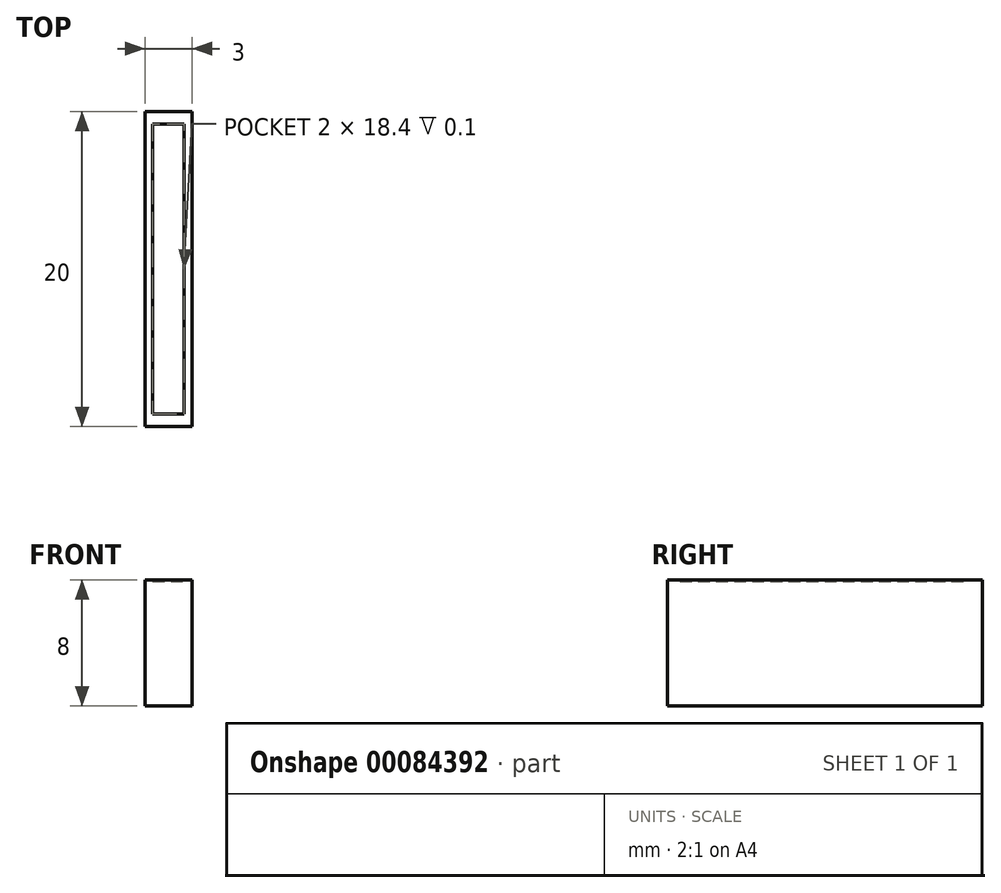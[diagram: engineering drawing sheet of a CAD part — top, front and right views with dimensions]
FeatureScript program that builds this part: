
annotation { "Feature Type Name" : "Feature", "Feature Type Description" : "" }
export const myFeature = defineFeature(function(context is Context, id is Id, definition is map)
    precondition{}
    {
        {
            var Q0;
            Q0=qCreatedBy(makeId("Top.planeOp"),FACE);
            var sketch = newSketch(context, id + "F0", { "sketchPlane" : qUnion([Q0])});
            skLineSegment(sketch, "E0.bottom", {"start": v(-53.44, 15.74) * mm, "end": v(-50.44, 15.74) * mm});
            skLineSegment(sketch, "E0.top", {"start": v(-53.44, -4.26) * mm, "end": v(-50.44, -4.26) * mm});
            skLineSegment(sketch, "E0.left", {"start": v(-53.44, 15.74) * mm, "end": v(-53.44, -4.26) * mm});
            skLineSegment(sketch, "E0.right", {"start": v(-50.44, 15.74) * mm, "end": v(-50.44, -4.26) * mm});
            skLineSegment(sketch, "E1", {"start": v(-50.94, -4.26) * mm, "end": v(-50.94, 15.74) * mm});
            skLineSegment(sketch, "E2", {"start": v(-52.94, -4.26) * mm, "end": v(-52.94, 15.74) * mm});
            skLineSegment(sketch, "E3", {"start": v(-52.94, -3.46) * mm, "end": v(-50.94, -3.46) * mm});
            skLineSegment(sketch, "E4", {"start": v(-52.94, -1.86) * mm, "end": v(-50.94, -1.86) * mm});
            skLineSegment(sketch, "E5", {"start": v(-52.94, -1.06) * mm, "end": v(-50.94, -1.06) * mm});
            skLineSegment(sketch, "E6", {"start": v(-52.94, 0.54) * mm, "end": v(-50.94, 0.54) * mm});
            skLineSegment(sketch, "E7", {"start": v(-52.94, 1.34) * mm, "end": v(-50.94, 1.34) * mm});
            skLineSegment(sketch, "E8", {"start": v(-52.94, 2.94) * mm, "end": v(-50.94, 2.94) * mm});
            skLineSegment(sketch, "E9", {"start": v(-52.94, 3.74) * mm, "end": v(-50.94, 3.74) * mm});
            skLineSegment(sketch, "E10", {"start": v(-52.94, 5.34) * mm, "end": v(-50.94, 5.34) * mm});
            skLineSegment(sketch, "E11", {"start": v(-52.94, 6.14) * mm, "end": v(-50.94, 6.14) * mm});
            skLineSegment(sketch, "E12", {"start": v(-52.94, 7.74) * mm, "end": v(-50.94, 7.74) * mm});
            skLineSegment(sketch, "E13", {"start": v(-52.94, 8.54) * mm, "end": v(-50.94, 8.54) * mm});
            skLineSegment(sketch, "E14", {"start": v(-52.94, 10.14) * mm, "end": v(-50.94, 10.14) * mm});
            skLineSegment(sketch, "E15", {"start": v(-52.94, 10.94) * mm, "end": v(-50.94, 10.94) * mm});
            skLineSegment(sketch, "E16", {"start": v(-52.94, 12.54) * mm, "end": v(-50.94, 12.54) * mm});
            skLineSegment(sketch, "E17", {"start": v(-52.94, 13.34) * mm, "end": v(-50.94, 13.34) * mm});
            skLineSegment(sketch, "E18", {"start": v(-52.94, 14.94) * mm, "end": v(-50.94, 14.94) * mm});
            skLineSegment(sketch, "E19", {"start": v(-52.94, 15.74) * mm, "end": v(-50.94, 15.74) * mm});
            skLineSegment(sketch, "E20", {"start": v(-52.94, -3.06) * mm, "end": v(-50.94, -3.06) * mm});
            skLineSegment(sketch, "E21", {"start": v(-52.94, -2.26) * mm, "end": v(-50.94, -2.26) * mm});
            skLineSegment(sketch, "E22", {"start": v(-52.54, -4.26) * mm, "end": v(-52.54, 15.74) * mm});
            skLineSegment(sketch, "E23", {"start": v(-51.34, -4.26) * mm, "end": v(-51.34, 15.74) * mm});
            skLineSegment(sketch, "E24", {"start": v(-51.34, 15.74) * mm, "end": v(-51.55, 15.82) * mm});
            skLineSegment(sketch, "E25", {"start": v(-52.94, -0.66) * mm, "end": v(-50.94, -0.66) * mm});
            skLineSegment(sketch, "E26", {"start": v(-52.94, 0.14) * mm, "end": v(-50.94, 0.14) * mm});
            skLineSegment(sketch, "E27", {"start": v(-52.94, 1.74) * mm, "end": v(-50.94, 1.74) * mm});
            skLineSegment(sketch, "E28", {"start": v(-52.94, 2.54) * mm, "end": v(-50.94, 2.54) * mm});
            skLineSegment(sketch, "E29", {"start": v(-52.94, 4.14) * mm, "end": v(-50.94, 4.14) * mm});
            skLineSegment(sketch, "E30", {"start": v(-52.94, 4.94) * mm, "end": v(-50.94, 4.94) * mm});
            skLineSegment(sketch, "E31", {"start": v(-52.94, 6.54) * mm, "end": v(-50.94, 6.54) * mm});
            skLineSegment(sketch, "E32", {"start": v(-52.94, 8.94) * mm, "end": v(-50.94, 8.94) * mm});
            skLineSegment(sketch, "E33", {"start": v(-52.94, 9.74) * mm, "end": v(-50.94, 9.74) * mm});
            skLineSegment(sketch, "E34", {"start": v(-52.94, 11.34) * mm, "end": v(-50.94, 11.34) * mm});
            skLineSegment(sketch, "E35", {"start": v(-50.94, 11.34) * mm, "end": v(-50.9, 11.2) * mm});
            skLineSegment(sketch, "E36", {"start": v(-52.94, 12.14) * mm, "end": v(-50.94, 12.14) * mm});
            skLineSegment(sketch, "E37", {"start": v(-52.94, 13.74) * mm, "end": v(-50.94, 13.74) * mm});
            skLineSegment(sketch, "E38", {"start": v(-52.94, 14.54) * mm, "end": v(-50.94, 14.54) * mm});
            skLineSegment(sketch, "E39", {"start": v(-52.94, 7.34) * mm, "end": v(-50.94, 7.34) * mm});
            skSolve(sketch);
        }
        {
            var Q0;
            Q0 = qSketchRegion(id + "F0", true);
            extrude(context, id + "F1", {"entities" : qUnion([Q0]), "depth" : 8 * mm});
        }
        {
            var Q0;
            {var subQ0=sQuery(id+"F0.wireOp",EDGE,"E18");var subQ1=sQuery(id+"F0.wireOp",EDGE,"E2");var subQ2=makeQuery(id+"F0.imprint","INTERSECT",VERTEX,{"derivedFrom":[subQ1,subQ0]});Q0=makeQuery(id+"F0.imprint","IMPRINT",FACE,{"disambiguationData":[TD([[makeQuery(id+"F0.imprint","IMPRINT",EDGE,{"disambiguationData":[TD([[subQ2,1.0]])],"derivedFrom":subQ1}),-1.0]])]});}
            var Q1;
            {var subQ0=sQuery(id+"F0.wireOp",EDGE,"E37");var subQ1=sQuery(id+"F0.wireOp",EDGE,"E2");var subQ2=makeQuery(id+"F0.imprint","INTERSECT",VERTEX,{"derivedFrom":[subQ1,subQ0]});Q1=makeQuery(id+"F0.imprint","IMPRINT",FACE,{"disambiguationData":[TD([[makeQuery(id+"F0.imprint","IMPRINT",EDGE,{"disambiguationData":[TD([[subQ2,-1.0]])],"derivedFrom":subQ1}),-1.0]])]});}
            var Q2;
            {var subQ0=sQuery(id+"F0.wireOp",EDGE,"E17");var subQ1=sQuery(id+"F0.wireOp",EDGE,"E2");var subQ2=makeQuery(id+"F0.imprint","INTERSECT",VERTEX,{"derivedFrom":[subQ1,subQ0]});Q2=makeQuery(id+"F0.imprint","IMPRINT",FACE,{"disambiguationData":[TD([[makeQuery(id+"F0.imprint","IMPRINT",EDGE,{"disambiguationData":[TD([[subQ2,-1.0]])],"derivedFrom":subQ1}),-1.0]])]});}
            var Q3;
            {var subQ0=sQuery(id+"F0.wireOp",EDGE,"E16");var subQ1=sQuery(id+"F0.wireOp",EDGE,"E2");var subQ2=makeQuery(id+"F0.imprint","INTERSECT",VERTEX,{"derivedFrom":[subQ1,subQ0]});Q3=makeQuery(id+"F0.imprint","IMPRINT",FACE,{"disambiguationData":[TD([[makeQuery(id+"F0.imprint","IMPRINT",EDGE,{"disambiguationData":[TD([[subQ2,-1.0]])],"derivedFrom":subQ1}),-1.0]])]});}
            var Q4;
            {var subQ0=sQuery(id+"F0.wireOp",EDGE,"E16");var subQ1=sQuery(id+"F0.wireOp",EDGE,"E2");var subQ2=makeQuery(id+"F0.imprint","INTERSECT",VERTEX,{"derivedFrom":[subQ1,subQ0]});Q4=makeQuery(id+"F0.imprint","IMPRINT",FACE,{"disambiguationData":[TD([[makeQuery(id+"F0.imprint","IMPRINT",EDGE,{"disambiguationData":[TD([[subQ2,1.0]])],"derivedFrom":subQ1}),-1.0]])]});}
            var Q5;
            {var subQ0=sQuery(id+"F0.wireOp",EDGE,"E34");var subQ1=sQuery(id+"F0.wireOp",EDGE,"E2");var subQ2=makeQuery(id+"F0.imprint","INTERSECT",VERTEX,{"derivedFrom":[subQ1,subQ0]});Q5=makeQuery(id+"F0.imprint","IMPRINT",FACE,{"disambiguationData":[TD([[makeQuery(id+"F0.imprint","IMPRINT",EDGE,{"disambiguationData":[TD([[subQ2,-1.0]])],"derivedFrom":subQ1}),-1.0]])]});}
            var Q6;
            {var subQ0=sQuery(id+"F0.wireOp",EDGE,"E15");var subQ1=sQuery(id+"F0.wireOp",EDGE,"E2");var subQ2=makeQuery(id+"F0.imprint","INTERSECT",VERTEX,{"derivedFrom":[subQ1,subQ0]});Q6=makeQuery(id+"F0.imprint","IMPRINT",FACE,{"disambiguationData":[TD([[makeQuery(id+"F0.imprint","IMPRINT",EDGE,{"disambiguationData":[TD([[subQ2,-1.0]])],"derivedFrom":subQ1}),-1.0]])]});}
            var Q7;
            {var subQ0=sQuery(id+"F0.wireOp",EDGE,"E14");var subQ1=sQuery(id+"F0.wireOp",EDGE,"E2");var subQ2=makeQuery(id+"F0.imprint","INTERSECT",VERTEX,{"derivedFrom":[subQ1,subQ0]});Q7=makeQuery(id+"F0.imprint","IMPRINT",FACE,{"disambiguationData":[TD([[makeQuery(id+"F0.imprint","IMPRINT",EDGE,{"disambiguationData":[TD([[subQ2,-1.0]])],"derivedFrom":subQ1}),-1.0]])]});}
            var Q8;
            {var subQ0=sQuery(id+"F0.wireOp",EDGE,"E14");var subQ1=sQuery(id+"F0.wireOp",EDGE,"E2");var subQ2=makeQuery(id+"F0.imprint","INTERSECT",VERTEX,{"derivedFrom":[subQ1,subQ0]});Q8=makeQuery(id+"F0.imprint","IMPRINT",FACE,{"disambiguationData":[TD([[makeQuery(id+"F0.imprint","IMPRINT",EDGE,{"disambiguationData":[TD([[subQ2,1.0]])],"derivedFrom":subQ1}),-1.0]])]});}
            var Q9;
            {var subQ0=sQuery(id+"F0.wireOp",EDGE,"E22");var subQ1=sQuery(id+"F0.wireOp",EDGE,"E14");var subQ2=makeQuery(id+"F0.imprint","INTERSECT",VERTEX,{"derivedFrom":[subQ1,subQ0]});Q9=makeQuery(id+"F0.imprint","IMPRINT",FACE,{"disambiguationData":[TD([[makeQuery(id+"F0.imprint","IMPRINT",EDGE,{"disambiguationData":[TD([[subQ2,-1.0]])],"derivedFrom":subQ1}),-1.0]])]});}
            var Q10;
            {var subQ0=sQuery(id+"F0.wireOp",EDGE,"E22");var subQ1=sQuery(id+"F0.wireOp",EDGE,"E15");var subQ2=makeQuery(id+"F0.imprint","INTERSECT",VERTEX,{"derivedFrom":[subQ1,subQ0]});Q10=makeQuery(id+"F0.imprint","IMPRINT",FACE,{"disambiguationData":[TD([[makeQuery(id+"F0.imprint","IMPRINT",EDGE,{"disambiguationData":[TD([[subQ2,-1.0]])],"derivedFrom":subQ1}),1.0]])]});}
            var Q11;
            {var subQ0=sQuery(id+"F0.wireOp",EDGE,"E22");var subQ1=sQuery(id+"F0.wireOp",EDGE,"E16");var subQ2=makeQuery(id+"F0.imprint","INTERSECT",VERTEX,{"derivedFrom":[subQ1,subQ0]});Q11=makeQuery(id+"F0.imprint","IMPRINT",FACE,{"disambiguationData":[TD([[makeQuery(id+"F0.imprint","IMPRINT",EDGE,{"disambiguationData":[TD([[subQ2,-1.0]])],"derivedFrom":subQ1}),-1.0]])]});}
            var Q12;
            {var subQ0=sQuery(id+"F0.wireOp",EDGE,"E22");var subQ1=sQuery(id+"F0.wireOp",EDGE,"E17");var subQ2=makeQuery(id+"F0.imprint","INTERSECT",VERTEX,{"derivedFrom":[subQ1,subQ0]});Q12=makeQuery(id+"F0.imprint","IMPRINT",FACE,{"disambiguationData":[TD([[makeQuery(id+"F0.imprint","IMPRINT",EDGE,{"disambiguationData":[TD([[subQ2,-1.0]])],"derivedFrom":subQ1}),1.0]])]});}
            var Q13;
            {var subQ0=sQuery(id+"F0.wireOp",EDGE,"E22");var subQ1=sQuery(id+"F0.wireOp",EDGE,"E18");var subQ2=makeQuery(id+"F0.imprint","INTERSECT",VERTEX,{"derivedFrom":[subQ1,subQ0]});Q13=makeQuery(id+"F0.imprint","IMPRINT",FACE,{"disambiguationData":[TD([[makeQuery(id+"F0.imprint","IMPRINT",EDGE,{"disambiguationData":[TD([[subQ2,-1.0]])],"derivedFrom":subQ1}),-1.0]])]});}
            var Q14;
            {var subQ0=sQuery(id+"F0.wireOp",EDGE,"E22");var subQ1=sQuery(id+"F0.wireOp",EDGE,"E3");var subQ2=makeQuery(id+"F0.imprint","INTERSECT",VERTEX,{"derivedFrom":[subQ1,subQ0]});Q14=makeQuery(id+"F0.imprint","IMPRINT",FACE,{"disambiguationData":[TD([[makeQuery(id+"F0.imprint","IMPRINT",EDGE,{"disambiguationData":[TD([[subQ2,-1.0]])],"derivedFrom":subQ1}),1.0]])]});}
            var Q15;
            {var subQ0=sQuery(id+"F0.wireOp",EDGE,"E22");var subQ1=sQuery(id+"F0.wireOp",EDGE,"E4");var subQ2=makeQuery(id+"F0.imprint","INTERSECT",VERTEX,{"derivedFrom":[subQ1,subQ0]});Q15=makeQuery(id+"F0.imprint","IMPRINT",FACE,{"disambiguationData":[TD([[makeQuery(id+"F0.imprint","IMPRINT",EDGE,{"disambiguationData":[TD([[subQ2,-1.0]])],"derivedFrom":subQ1}),-1.0]])]});}
            var Q16;
            {var subQ0=sQuery(id+"F0.wireOp",EDGE,"E22");var subQ1=sQuery(id+"F0.wireOp",EDGE,"E5");var subQ2=makeQuery(id+"F0.imprint","INTERSECT",VERTEX,{"derivedFrom":[subQ1,subQ0]});Q16=makeQuery(id+"F0.imprint","IMPRINT",FACE,{"disambiguationData":[TD([[makeQuery(id+"F0.imprint","IMPRINT",EDGE,{"disambiguationData":[TD([[subQ2,-1.0]])],"derivedFrom":subQ1}),1.0]])]});}
            var Q17;
            {var subQ0=sQuery(id+"F0.wireOp",EDGE,"E22");var subQ1=sQuery(id+"F0.wireOp",EDGE,"E6");var subQ2=makeQuery(id+"F0.imprint","INTERSECT",VERTEX,{"derivedFrom":[subQ1,subQ0]});Q17=makeQuery(id+"F0.imprint","IMPRINT",FACE,{"disambiguationData":[TD([[makeQuery(id+"F0.imprint","IMPRINT",EDGE,{"disambiguationData":[TD([[subQ2,-1.0]])],"derivedFrom":subQ1}),-1.0]])]});}
            var Q18;
            {var subQ0=sQuery(id+"F0.wireOp",EDGE,"E22");var subQ1=sQuery(id+"F0.wireOp",EDGE,"E7");var subQ2=makeQuery(id+"F0.imprint","INTERSECT",VERTEX,{"derivedFrom":[subQ1,subQ0]});Q18=makeQuery(id+"F0.imprint","IMPRINT",FACE,{"disambiguationData":[TD([[makeQuery(id+"F0.imprint","IMPRINT",EDGE,{"disambiguationData":[TD([[subQ2,-1.0]])],"derivedFrom":subQ1}),1.0]])]});}
            var Q19;
            {var subQ0=sQuery(id+"F0.wireOp",EDGE,"E22");var subQ1=sQuery(id+"F0.wireOp",EDGE,"E8");var subQ2=makeQuery(id+"F0.imprint","INTERSECT",VERTEX,{"derivedFrom":[subQ1,subQ0]});Q19=makeQuery(id+"F0.imprint","IMPRINT",FACE,{"disambiguationData":[TD([[makeQuery(id+"F0.imprint","IMPRINT",EDGE,{"disambiguationData":[TD([[subQ2,-1.0]])],"derivedFrom":subQ1}),-1.0]])]});}
            var Q20;
            {var subQ0=sQuery(id+"F0.wireOp",EDGE,"E9");var subQ1=sQuery(id+"F0.wireOp",EDGE,"E22");var subQ2=makeQuery(id+"F0.imprint","INTERSECT",VERTEX,{"derivedFrom":[subQ1,subQ0]});Q20=makeQuery(id+"F0.imprint","IMPRINT",FACE,{"disambiguationData":[TD([[makeQuery(id+"F0.imprint","IMPRINT",EDGE,{"disambiguationData":[TD([[subQ2,-1.0]])],"derivedFrom":subQ1}),-1.0]])]});}
            var Q21;
            {var subQ0=sQuery(id+"F0.wireOp",EDGE,"E22");var subQ1=sQuery(id+"F0.wireOp",EDGE,"E10");var subQ2=makeQuery(id+"F0.imprint","INTERSECT",VERTEX,{"derivedFrom":[subQ1,subQ0]});Q21=makeQuery(id+"F0.imprint","IMPRINT",FACE,{"disambiguationData":[TD([[makeQuery(id+"F0.imprint","IMPRINT",EDGE,{"disambiguationData":[TD([[subQ2,-1.0]])],"derivedFrom":subQ1}),-1.0]])]});}
            var Q22;
            {var subQ0=sQuery(id+"F0.wireOp",EDGE,"E22");var subQ1=sQuery(id+"F0.wireOp",EDGE,"E11");var subQ2=makeQuery(id+"F0.imprint","INTERSECT",VERTEX,{"derivedFrom":[subQ1,subQ0]});Q22=makeQuery(id+"F0.imprint","IMPRINT",FACE,{"disambiguationData":[TD([[makeQuery(id+"F0.imprint","IMPRINT",EDGE,{"disambiguationData":[TD([[subQ2,-1.0]])],"derivedFrom":subQ1}),1.0]])]});}
            var Q23;
            {var subQ0=sQuery(id+"F0.wireOp",EDGE,"E22");var subQ1=sQuery(id+"F0.wireOp",EDGE,"E12");var subQ2=makeQuery(id+"F0.imprint","INTERSECT",VERTEX,{"derivedFrom":[subQ1,subQ0]});Q23=makeQuery(id+"F0.imprint","IMPRINT",FACE,{"disambiguationData":[TD([[makeQuery(id+"F0.imprint","IMPRINT",EDGE,{"disambiguationData":[TD([[subQ2,-1.0]])],"derivedFrom":subQ1}),-1.0]])]});}
            var Q24;
            {var subQ0=sQuery(id+"F0.wireOp",EDGE,"E22");var subQ1=sQuery(id+"F0.wireOp",EDGE,"E13");var subQ2=makeQuery(id+"F0.imprint","INTERSECT",VERTEX,{"derivedFrom":[subQ1,subQ0]});Q24=makeQuery(id+"F0.imprint","IMPRINT",FACE,{"disambiguationData":[TD([[makeQuery(id+"F0.imprint","IMPRINT",EDGE,{"disambiguationData":[TD([[subQ2,-1.0]])],"derivedFrom":subQ1}),1.0]])]});}
            var Q25;
            {var subQ0=sQuery(id+"F0.wireOp",EDGE,"E18");var subQ1=sQuery(id+"F0.wireOp",EDGE,"E1");var subQ2=makeQuery(id+"F0.imprint","INTERSECT",VERTEX,{"derivedFrom":[subQ1,subQ0]});Q25=makeQuery(id+"F0.imprint","IMPRINT",FACE,{"disambiguationData":[TD([[makeQuery(id+"F0.imprint","IMPRINT",EDGE,{"disambiguationData":[TD([[subQ2,1.0]])],"derivedFrom":subQ1}),1.0]])]});}
            var Q26;
            {var subQ0=sQuery(id+"F0.wireOp",EDGE,"E17");var subQ1=sQuery(id+"F0.wireOp",EDGE,"E1");var subQ2=makeQuery(id+"F0.imprint","INTERSECT",VERTEX,{"derivedFrom":[subQ1,subQ0]});Q26=makeQuery(id+"F0.imprint","IMPRINT",FACE,{"disambiguationData":[TD([[makeQuery(id+"F0.imprint","IMPRINT",EDGE,{"disambiguationData":[TD([[subQ2,-1.0]])],"derivedFrom":subQ1}),1.0]])]});}
            var Q27;
            {var subQ0=sQuery(id+"F0.wireOp",EDGE,"E16");var subQ1=sQuery(id+"F0.wireOp",EDGE,"E1");var subQ2=makeQuery(id+"F0.imprint","INTERSECT",VERTEX,{"derivedFrom":[subQ1,subQ0]});Q27=makeQuery(id+"F0.imprint","IMPRINT",FACE,{"disambiguationData":[TD([[makeQuery(id+"F0.imprint","IMPRINT",EDGE,{"disambiguationData":[TD([[subQ2,1.0]])],"derivedFrom":subQ1}),1.0]])]});}
            var Q28;
            {var subQ0=sQuery(id+"F0.wireOp",EDGE,"E15");var subQ1=sQuery(id+"F0.wireOp",EDGE,"E1");var subQ2=makeQuery(id+"F0.imprint","INTERSECT",VERTEX,{"derivedFrom":[subQ1,subQ0]});Q28=makeQuery(id+"F0.imprint","IMPRINT",FACE,{"disambiguationData":[TD([[makeQuery(id+"F0.imprint","IMPRINT",EDGE,{"disambiguationData":[TD([[subQ2,-1.0]])],"derivedFrom":subQ1}),1.0]])]});}
            var Q29;
            {var subQ0=sQuery(id+"F0.wireOp",EDGE,"E14");var subQ1=sQuery(id+"F0.wireOp",EDGE,"E1");var subQ2=makeQuery(id+"F0.imprint","INTERSECT",VERTEX,{"derivedFrom":[subQ1,subQ0]});Q29=makeQuery(id+"F0.imprint","IMPRINT",FACE,{"disambiguationData":[TD([[makeQuery(id+"F0.imprint","IMPRINT",EDGE,{"disambiguationData":[TD([[subQ2,1.0]])],"derivedFrom":subQ1}),1.0]])]});}
            var Q30;
            {var subQ0=sQuery(id+"F0.wireOp",EDGE,"E13");var subQ1=sQuery(id+"F0.wireOp",EDGE,"E1");var subQ2=makeQuery(id+"F0.imprint","INTERSECT",VERTEX,{"derivedFrom":[subQ1,subQ0]});Q30=makeQuery(id+"F0.imprint","IMPRINT",FACE,{"disambiguationData":[TD([[makeQuery(id+"F0.imprint","IMPRINT",EDGE,{"disambiguationData":[TD([[subQ2,-1.0]])],"derivedFrom":subQ1}),1.0]])]});}
            var Q31;
            {var subQ0=sQuery(id+"F0.wireOp",EDGE,"E12");var subQ1=sQuery(id+"F0.wireOp",EDGE,"E1");var subQ2=makeQuery(id+"F0.imprint","INTERSECT",VERTEX,{"derivedFrom":[subQ1,subQ0]});Q31=makeQuery(id+"F0.imprint","IMPRINT",FACE,{"disambiguationData":[TD([[makeQuery(id+"F0.imprint","IMPRINT",EDGE,{"disambiguationData":[TD([[subQ2,1.0]])],"derivedFrom":subQ1}),1.0]])]});}
            var Q32;
            {var subQ0=sQuery(id+"F0.wireOp",EDGE,"E11");var subQ1=sQuery(id+"F0.wireOp",EDGE,"E1");var subQ2=makeQuery(id+"F0.imprint","INTERSECT",VERTEX,{"derivedFrom":[subQ1,subQ0]});Q32=makeQuery(id+"F0.imprint","IMPRINT",FACE,{"disambiguationData":[TD([[makeQuery(id+"F0.imprint","IMPRINT",EDGE,{"disambiguationData":[TD([[subQ2,-1.0]])],"derivedFrom":subQ1}),1.0]])]});}
            var Q33;
            {var subQ0=sQuery(id+"F0.wireOp",EDGE,"E10");var subQ1=sQuery(id+"F0.wireOp",EDGE,"E1");var subQ2=makeQuery(id+"F0.imprint","INTERSECT",VERTEX,{"derivedFrom":[subQ1,subQ0]});Q33=makeQuery(id+"F0.imprint","IMPRINT",FACE,{"disambiguationData":[TD([[makeQuery(id+"F0.imprint","IMPRINT",EDGE,{"disambiguationData":[TD([[subQ2,1.0]])],"derivedFrom":subQ1}),1.0]])]});}
            var Q34;
            {var subQ0=sQuery(id+"F0.wireOp",EDGE,"E29");var subQ1=sQuery(id+"F0.wireOp",EDGE,"E1");var subQ2=makeQuery(id+"F0.imprint","INTERSECT",VERTEX,{"derivedFrom":[subQ1,subQ0]});Q34=makeQuery(id+"F0.imprint","IMPRINT",FACE,{"disambiguationData":[TD([[makeQuery(id+"F0.imprint","IMPRINT",EDGE,{"disambiguationData":[TD([[subQ2,1.0]])],"derivedFrom":subQ1}),1.0]])]});}
            var Q35;
            {var subQ0=sQuery(id+"F0.wireOp",EDGE,"E8");var subQ1=sQuery(id+"F0.wireOp",EDGE,"E1");var subQ2=makeQuery(id+"F0.imprint","INTERSECT",VERTEX,{"derivedFrom":[subQ1,subQ0]});Q35=makeQuery(id+"F0.imprint","IMPRINT",FACE,{"disambiguationData":[TD([[makeQuery(id+"F0.imprint","IMPRINT",EDGE,{"disambiguationData":[TD([[subQ2,1.0]])],"derivedFrom":subQ1}),1.0]])]});}
            var Q36;
            {var subQ0=sQuery(id+"F0.wireOp",EDGE,"E7");var subQ1=sQuery(id+"F0.wireOp",EDGE,"E1");var subQ2=makeQuery(id+"F0.imprint","INTERSECT",VERTEX,{"derivedFrom":[subQ1,subQ0]});Q36=makeQuery(id+"F0.imprint","IMPRINT",FACE,{"disambiguationData":[TD([[makeQuery(id+"F0.imprint","IMPRINT",EDGE,{"disambiguationData":[TD([[subQ2,-1.0]])],"derivedFrom":subQ1}),1.0]])]});}
            var Q37;
            {var subQ0=sQuery(id+"F0.wireOp",EDGE,"E6");var subQ1=sQuery(id+"F0.wireOp",EDGE,"E1");var subQ2=makeQuery(id+"F0.imprint","INTERSECT",VERTEX,{"derivedFrom":[subQ1,subQ0]});Q37=makeQuery(id+"F0.imprint","IMPRINT",FACE,{"disambiguationData":[TD([[makeQuery(id+"F0.imprint","IMPRINT",EDGE,{"disambiguationData":[TD([[subQ2,1.0]])],"derivedFrom":subQ1}),1.0]])]});}
            var Q38;
            {var subQ0=sQuery(id+"F0.wireOp",EDGE,"E5");var subQ1=sQuery(id+"F0.wireOp",EDGE,"E1");var subQ2=makeQuery(id+"F0.imprint","INTERSECT",VERTEX,{"derivedFrom":[subQ1,subQ0]});Q38=makeQuery(id+"F0.imprint","IMPRINT",FACE,{"disambiguationData":[TD([[makeQuery(id+"F0.imprint","IMPRINT",EDGE,{"disambiguationData":[TD([[subQ2,-1.0]])],"derivedFrom":subQ1}),1.0]])]});}
            var Q39;
            {var subQ0=sQuery(id+"F0.wireOp",EDGE,"E4");var subQ1=sQuery(id+"F0.wireOp",EDGE,"E1");var subQ2=makeQuery(id+"F0.imprint","INTERSECT",VERTEX,{"derivedFrom":[subQ1,subQ0]});Q39=makeQuery(id+"F0.imprint","IMPRINT",FACE,{"disambiguationData":[TD([[makeQuery(id+"F0.imprint","IMPRINT",EDGE,{"disambiguationData":[TD([[subQ2,1.0]])],"derivedFrom":subQ1}),1.0]])]});}
            var Q40;
            {var subQ0=sQuery(id+"F0.wireOp",EDGE,"E3");var subQ1=sQuery(id+"F0.wireOp",EDGE,"E1");var subQ2=makeQuery(id+"F0.imprint","INTERSECT",VERTEX,{"derivedFrom":[subQ1,subQ0]});Q40=makeQuery(id+"F0.imprint","IMPRINT",FACE,{"disambiguationData":[TD([[makeQuery(id+"F0.imprint","IMPRINT",EDGE,{"disambiguationData":[TD([[subQ2,-1.0]])],"derivedFrom":subQ1}),1.0]])]});}
            var Q41;
            {var subQ0=sQuery(id+"F0.wireOp",EDGE,"E3");var subQ1=sQuery(id+"F0.wireOp",EDGE,"E2");var subQ2=makeQuery(id+"F0.imprint","INTERSECT",VERTEX,{"derivedFrom":[subQ1,subQ0]});Q41=makeQuery(id+"F0.imprint","IMPRINT",FACE,{"disambiguationData":[TD([[makeQuery(id+"F0.imprint","IMPRINT",EDGE,{"disambiguationData":[TD([[subQ2,-1.0]])],"derivedFrom":subQ1}),-1.0]])]});}
            var Q42;
            {var subQ0=sQuery(id+"F0.wireOp",EDGE,"E4");var subQ1=sQuery(id+"F0.wireOp",EDGE,"E2");var subQ2=makeQuery(id+"F0.imprint","INTERSECT",VERTEX,{"derivedFrom":[subQ1,subQ0]});Q42=makeQuery(id+"F0.imprint","IMPRINT",FACE,{"disambiguationData":[TD([[makeQuery(id+"F0.imprint","IMPRINT",EDGE,{"disambiguationData":[TD([[subQ2,1.0]])],"derivedFrom":subQ1}),-1.0]])]});}
            var Q43;
            {var subQ0=sQuery(id+"F0.wireOp",EDGE,"E5");var subQ1=sQuery(id+"F0.wireOp",EDGE,"E2");var subQ2=makeQuery(id+"F0.imprint","INTERSECT",VERTEX,{"derivedFrom":[subQ1,subQ0]});Q43=makeQuery(id+"F0.imprint","IMPRINT",FACE,{"disambiguationData":[TD([[makeQuery(id+"F0.imprint","IMPRINT",EDGE,{"disambiguationData":[TD([[subQ2,-1.0]])],"derivedFrom":subQ1}),-1.0]])]});}
            var Q44;
            {var subQ0=sQuery(id+"F0.wireOp",EDGE,"E6");var subQ1=sQuery(id+"F0.wireOp",EDGE,"E2");var subQ2=makeQuery(id+"F0.imprint","INTERSECT",VERTEX,{"derivedFrom":[subQ1,subQ0]});Q44=makeQuery(id+"F0.imprint","IMPRINT",FACE,{"disambiguationData":[TD([[makeQuery(id+"F0.imprint","IMPRINT",EDGE,{"disambiguationData":[TD([[subQ2,1.0]])],"derivedFrom":subQ1}),-1.0]])]});}
            var Q45;
            {var subQ0=sQuery(id+"F0.wireOp",EDGE,"E7");var subQ1=sQuery(id+"F0.wireOp",EDGE,"E2");var subQ2=makeQuery(id+"F0.imprint","INTERSECT",VERTEX,{"derivedFrom":[subQ1,subQ0]});Q45=makeQuery(id+"F0.imprint","IMPRINT",FACE,{"disambiguationData":[TD([[makeQuery(id+"F0.imprint","IMPRINT",EDGE,{"disambiguationData":[TD([[subQ2,-1.0]])],"derivedFrom":subQ1}),-1.0]])]});}
            var Q46;
            {var subQ0=sQuery(id+"F0.wireOp",EDGE,"E8");var subQ1=sQuery(id+"F0.wireOp",EDGE,"E2");var subQ2=makeQuery(id+"F0.imprint","INTERSECT",VERTEX,{"derivedFrom":[subQ1,subQ0]});Q46=makeQuery(id+"F0.imprint","IMPRINT",FACE,{"disambiguationData":[TD([[makeQuery(id+"F0.imprint","IMPRINT",EDGE,{"disambiguationData":[TD([[subQ2,1.0]])],"derivedFrom":subQ1}),-1.0]])]});}
            var Q47;
            {var subQ0=sQuery(id+"F0.wireOp",EDGE,"E29");var subQ1=sQuery(id+"F0.wireOp",EDGE,"E2");var subQ2=makeQuery(id+"F0.imprint","INTERSECT",VERTEX,{"derivedFrom":[subQ1,subQ0]});Q47=makeQuery(id+"F0.imprint","IMPRINT",FACE,{"disambiguationData":[TD([[makeQuery(id+"F0.imprint","IMPRINT",EDGE,{"disambiguationData":[TD([[subQ2,1.0]])],"derivedFrom":subQ1}),-1.0]])]});}
            var Q48;
            {var subQ0=sQuery(id+"F0.wireOp",EDGE,"E10");var subQ1=sQuery(id+"F0.wireOp",EDGE,"E2");var subQ2=makeQuery(id+"F0.imprint","INTERSECT",VERTEX,{"derivedFrom":[subQ1,subQ0]});Q48=makeQuery(id+"F0.imprint","IMPRINT",FACE,{"disambiguationData":[TD([[makeQuery(id+"F0.imprint","IMPRINT",EDGE,{"disambiguationData":[TD([[subQ2,1.0]])],"derivedFrom":subQ1}),-1.0]])]});}
            var Q49;
            {var subQ0=sQuery(id+"F0.wireOp",EDGE,"E11");var subQ1=sQuery(id+"F0.wireOp",EDGE,"E2");var subQ2=makeQuery(id+"F0.imprint","INTERSECT",VERTEX,{"derivedFrom":[subQ1,subQ0]});Q49=makeQuery(id+"F0.imprint","IMPRINT",FACE,{"disambiguationData":[TD([[makeQuery(id+"F0.imprint","IMPRINT",EDGE,{"disambiguationData":[TD([[subQ2,-1.0]])],"derivedFrom":subQ1}),-1.0]])]});}
            var Q50;
            {var subQ0=sQuery(id+"F0.wireOp",EDGE,"E12");var subQ1=sQuery(id+"F0.wireOp",EDGE,"E2");var subQ2=makeQuery(id+"F0.imprint","INTERSECT",VERTEX,{"derivedFrom":[subQ1,subQ0]});Q50=makeQuery(id+"F0.imprint","IMPRINT",FACE,{"disambiguationData":[TD([[makeQuery(id+"F0.imprint","IMPRINT",EDGE,{"disambiguationData":[TD([[subQ2,1.0]])],"derivedFrom":subQ1}),-1.0]])]});}
            var Q51;
            {var subQ0=sQuery(id+"F0.wireOp",EDGE,"E13");var subQ1=sQuery(id+"F0.wireOp",EDGE,"E2");var subQ2=makeQuery(id+"F0.imprint","INTERSECT",VERTEX,{"derivedFrom":[subQ1,subQ0]});Q51=makeQuery(id+"F0.imprint","IMPRINT",FACE,{"disambiguationData":[TD([[makeQuery(id+"F0.imprint","IMPRINT",EDGE,{"disambiguationData":[TD([[subQ2,-1.0]])],"derivedFrom":subQ1}),-1.0]])]});}
            var Q52;
            {var subQ0=sQuery(id+"F0.wireOp",EDGE,"E37");var subQ1=sQuery(id+"F0.wireOp",EDGE,"E1");var subQ2=makeQuery(id+"F0.imprint","INTERSECT",VERTEX,{"derivedFrom":[subQ1,subQ0]});Q52=makeQuery(id+"F0.imprint","IMPRINT",FACE,{"disambiguationData":[TD([[makeQuery(id+"F0.imprint","IMPRINT",EDGE,{"disambiguationData":[TD([[subQ2,-1.0]])],"derivedFrom":subQ1}),1.0]])]});}
            var Q53;
            {var subQ0=sQuery(id+"F0.wireOp",EDGE,"E16");var subQ1=sQuery(id+"F0.wireOp",EDGE,"E1");var subQ2=makeQuery(id+"F0.imprint","INTERSECT",VERTEX,{"derivedFrom":[subQ1,subQ0]});Q53=makeQuery(id+"F0.imprint","IMPRINT",FACE,{"disambiguationData":[TD([[makeQuery(id+"F0.imprint","IMPRINT",EDGE,{"disambiguationData":[TD([[subQ2,-1.0]])],"derivedFrom":subQ1}),1.0]])]});}
            var Q54;
            {var subQ0=sQuery(id+"F0.wireOp",EDGE,"E34");var subQ1=sQuery(id+"F0.wireOp",EDGE,"E1");var subQ2=makeQuery(id+"F0.imprint","INTERSECT",VERTEX,{"derivedFrom":[subQ1,subQ0]});Q54=makeQuery(id+"F0.imprint","IMPRINT",FACE,{"disambiguationData":[TD([[makeQuery(id+"F0.imprint","IMPRINT",EDGE,{"disambiguationData":[TD([[subQ2,-1.0]])],"derivedFrom":subQ1}),1.0]])]});}
            var Q55;
            {var subQ0=sQuery(id+"F0.wireOp",EDGE,"E14");var subQ1=sQuery(id+"F0.wireOp",EDGE,"E1");var subQ2=makeQuery(id+"F0.imprint","INTERSECT",VERTEX,{"derivedFrom":[subQ1,subQ0]});Q55=makeQuery(id+"F0.imprint","IMPRINT",FACE,{"disambiguationData":[TD([[makeQuery(id+"F0.imprint","IMPRINT",EDGE,{"disambiguationData":[TD([[subQ2,-1.0]])],"derivedFrom":subQ1}),1.0]])]});}
            var Q56;
            {var subQ0=sQuery(id+"F0.wireOp",EDGE,"E32");var subQ1=sQuery(id+"F0.wireOp",EDGE,"E1");var subQ2=makeQuery(id+"F0.imprint","INTERSECT",VERTEX,{"derivedFrom":[subQ1,subQ0]});Q56=makeQuery(id+"F0.imprint","IMPRINT",FACE,{"disambiguationData":[TD([[makeQuery(id+"F0.imprint","IMPRINT",EDGE,{"disambiguationData":[TD([[subQ2,-1.0]])],"derivedFrom":subQ1}),1.0]])]});}
            var Q57;
            {var subQ0=sQuery(id+"F0.wireOp",EDGE,"E32");var subQ1=sQuery(id+"F0.wireOp",EDGE,"E2");var subQ2=makeQuery(id+"F0.imprint","INTERSECT",VERTEX,{"derivedFrom":[subQ1,subQ0]});Q57=makeQuery(id+"F0.imprint","IMPRINT",FACE,{"disambiguationData":[TD([[makeQuery(id+"F0.imprint","IMPRINT",EDGE,{"disambiguationData":[TD([[subQ2,-1.0]])],"derivedFrom":subQ1}),-1.0]])]});}
            var Q58;
            {var subQ0=sQuery(id+"F0.wireOp",EDGE,"E12");var subQ1=sQuery(id+"F0.wireOp",EDGE,"E2");var subQ2=makeQuery(id+"F0.imprint","INTERSECT",VERTEX,{"derivedFrom":[subQ1,subQ0]});Q58=makeQuery(id+"F0.imprint","IMPRINT",FACE,{"disambiguationData":[TD([[makeQuery(id+"F0.imprint","IMPRINT",EDGE,{"disambiguationData":[TD([[subQ2,-1.0]])],"derivedFrom":subQ1}),-1.0]])]});}
            var Q59;
            {var subQ0=sQuery(id+"F0.wireOp",EDGE,"E12");var subQ1=sQuery(id+"F0.wireOp",EDGE,"E1");var subQ2=makeQuery(id+"F0.imprint","INTERSECT",VERTEX,{"derivedFrom":[subQ1,subQ0]});Q59=makeQuery(id+"F0.imprint","IMPRINT",FACE,{"disambiguationData":[TD([[makeQuery(id+"F0.imprint","IMPRINT",EDGE,{"disambiguationData":[TD([[subQ2,-1.0]])],"derivedFrom":subQ1}),1.0]])]});}
            var Q60;
            {var subQ0=sQuery(id+"F0.wireOp",EDGE,"E31");var subQ1=sQuery(id+"F0.wireOp",EDGE,"E1");var subQ2=makeQuery(id+"F0.imprint","INTERSECT",VERTEX,{"derivedFrom":[subQ1,subQ0]});Q60=makeQuery(id+"F0.imprint","IMPRINT",FACE,{"disambiguationData":[TD([[makeQuery(id+"F0.imprint","IMPRINT",EDGE,{"disambiguationData":[TD([[subQ2,-1.0]])],"derivedFrom":subQ1}),1.0]])]});}
            var Q61;
            {var subQ0=sQuery(id+"F0.wireOp",EDGE,"E31");var subQ1=sQuery(id+"F0.wireOp",EDGE,"E2");var subQ2=makeQuery(id+"F0.imprint","INTERSECT",VERTEX,{"derivedFrom":[subQ1,subQ0]});Q61=makeQuery(id+"F0.imprint","IMPRINT",FACE,{"disambiguationData":[TD([[makeQuery(id+"F0.imprint","IMPRINT",EDGE,{"disambiguationData":[TD([[subQ2,-1.0]])],"derivedFrom":subQ1}),-1.0]])]});}
            var Q62;
            {var subQ0=sQuery(id+"F0.wireOp",EDGE,"E10");var subQ1=sQuery(id+"F0.wireOp",EDGE,"E2");var subQ2=makeQuery(id+"F0.imprint","INTERSECT",VERTEX,{"derivedFrom":[subQ1,subQ0]});Q62=makeQuery(id+"F0.imprint","IMPRINT",FACE,{"disambiguationData":[TD([[makeQuery(id+"F0.imprint","IMPRINT",EDGE,{"disambiguationData":[TD([[subQ2,-1.0]])],"derivedFrom":subQ1}),-1.0]])]});}
            var Q63;
            {var subQ0=sQuery(id+"F0.wireOp",EDGE,"E10");var subQ1=sQuery(id+"F0.wireOp",EDGE,"E1");var subQ2=makeQuery(id+"F0.imprint","INTERSECT",VERTEX,{"derivedFrom":[subQ1,subQ0]});Q63=makeQuery(id+"F0.imprint","IMPRINT",FACE,{"disambiguationData":[TD([[makeQuery(id+"F0.imprint","IMPRINT",EDGE,{"disambiguationData":[TD([[subQ2,-1.0]])],"derivedFrom":subQ1}),1.0]])]});}
            var Q64;
            {var subQ0=sQuery(id+"F0.wireOp",EDGE,"E29");var subQ1=sQuery(id+"F0.wireOp",EDGE,"E1");var subQ2=makeQuery(id+"F0.imprint","INTERSECT",VERTEX,{"derivedFrom":[subQ1,subQ0]});Q64=makeQuery(id+"F0.imprint","IMPRINT",FACE,{"disambiguationData":[TD([[makeQuery(id+"F0.imprint","IMPRINT",EDGE,{"disambiguationData":[TD([[subQ2,-1.0]])],"derivedFrom":subQ1}),1.0]])]});}
            var Q65;
            {var subQ0=sQuery(id+"F0.wireOp",EDGE,"E29");var subQ1=sQuery(id+"F0.wireOp",EDGE,"E2");var subQ2=makeQuery(id+"F0.imprint","INTERSECT",VERTEX,{"derivedFrom":[subQ1,subQ0]});Q65=makeQuery(id+"F0.imprint","IMPRINT",FACE,{"disambiguationData":[TD([[makeQuery(id+"F0.imprint","IMPRINT",EDGE,{"disambiguationData":[TD([[subQ2,-1.0]])],"derivedFrom":subQ1}),-1.0]])]});}
            var Q66;
            {var subQ0=sQuery(id+"F0.wireOp",EDGE,"E8");var subQ1=sQuery(id+"F0.wireOp",EDGE,"E2");var subQ2=makeQuery(id+"F0.imprint","INTERSECT",VERTEX,{"derivedFrom":[subQ1,subQ0]});Q66=makeQuery(id+"F0.imprint","IMPRINT",FACE,{"disambiguationData":[TD([[makeQuery(id+"F0.imprint","IMPRINT",EDGE,{"disambiguationData":[TD([[subQ2,-1.0]])],"derivedFrom":subQ1}),-1.0]])]});}
            var Q67;
            {var subQ0=sQuery(id+"F0.wireOp",EDGE,"E8");var subQ1=sQuery(id+"F0.wireOp",EDGE,"E1");var subQ2=makeQuery(id+"F0.imprint","INTERSECT",VERTEX,{"derivedFrom":[subQ1,subQ0]});Q67=makeQuery(id+"F0.imprint","IMPRINT",FACE,{"disambiguationData":[TD([[makeQuery(id+"F0.imprint","IMPRINT",EDGE,{"disambiguationData":[TD([[subQ2,-1.0]])],"derivedFrom":subQ1}),1.0]])]});}
            var Q68;
            {var subQ0=sQuery(id+"F0.wireOp",EDGE,"E27");var subQ1=sQuery(id+"F0.wireOp",EDGE,"E1");var subQ2=makeQuery(id+"F0.imprint","INTERSECT",VERTEX,{"derivedFrom":[subQ1,subQ0]});Q68=makeQuery(id+"F0.imprint","IMPRINT",FACE,{"disambiguationData":[TD([[makeQuery(id+"F0.imprint","IMPRINT",EDGE,{"disambiguationData":[TD([[subQ2,-1.0]])],"derivedFrom":subQ1}),1.0]])]});}
            var Q69;
            {var subQ0=sQuery(id+"F0.wireOp",EDGE,"E27");var subQ1=sQuery(id+"F0.wireOp",EDGE,"E2");var subQ2=makeQuery(id+"F0.imprint","INTERSECT",VERTEX,{"derivedFrom":[subQ1,subQ0]});Q69=makeQuery(id+"F0.imprint","IMPRINT",FACE,{"disambiguationData":[TD([[makeQuery(id+"F0.imprint","IMPRINT",EDGE,{"disambiguationData":[TD([[subQ2,-1.0]])],"derivedFrom":subQ1}),-1.0]])]});}
            var Q70;
            {var subQ0=sQuery(id+"F0.wireOp",EDGE,"E6");var subQ1=sQuery(id+"F0.wireOp",EDGE,"E2");var subQ2=makeQuery(id+"F0.imprint","INTERSECT",VERTEX,{"derivedFrom":[subQ1,subQ0]});Q70=makeQuery(id+"F0.imprint","IMPRINT",FACE,{"disambiguationData":[TD([[makeQuery(id+"F0.imprint","IMPRINT",EDGE,{"disambiguationData":[TD([[subQ2,-1.0]])],"derivedFrom":subQ1}),-1.0]])]});}
            var Q71;
            {var subQ0=sQuery(id+"F0.wireOp",EDGE,"E6");var subQ1=sQuery(id+"F0.wireOp",EDGE,"E1");var subQ2=makeQuery(id+"F0.imprint","INTERSECT",VERTEX,{"derivedFrom":[subQ1,subQ0]});Q71=makeQuery(id+"F0.imprint","IMPRINT",FACE,{"disambiguationData":[TD([[makeQuery(id+"F0.imprint","IMPRINT",EDGE,{"disambiguationData":[TD([[subQ2,-1.0]])],"derivedFrom":subQ1}),1.0]])]});}
            var Q72;
            {var subQ0=sQuery(id+"F0.wireOp",EDGE,"E25");var subQ1=sQuery(id+"F0.wireOp",EDGE,"E1");var subQ2=makeQuery(id+"F0.imprint","INTERSECT",VERTEX,{"derivedFrom":[subQ1,subQ0]});Q72=makeQuery(id+"F0.imprint","IMPRINT",FACE,{"disambiguationData":[TD([[makeQuery(id+"F0.imprint","IMPRINT",EDGE,{"disambiguationData":[TD([[subQ2,-1.0]])],"derivedFrom":subQ1}),1.0]])]});}
            var Q73;
            {var subQ0=sQuery(id+"F0.wireOp",EDGE,"E25");var subQ1=sQuery(id+"F0.wireOp",EDGE,"E2");var subQ2=makeQuery(id+"F0.imprint","INTERSECT",VERTEX,{"derivedFrom":[subQ1,subQ0]});Q73=makeQuery(id+"F0.imprint","IMPRINT",FACE,{"disambiguationData":[TD([[makeQuery(id+"F0.imprint","IMPRINT",EDGE,{"disambiguationData":[TD([[subQ2,-1.0]])],"derivedFrom":subQ1}),-1.0]])]});}
            var Q74;
            {var subQ0=sQuery(id+"F0.wireOp",EDGE,"E4");var subQ1=sQuery(id+"F0.wireOp",EDGE,"E2");var subQ2=makeQuery(id+"F0.imprint","INTERSECT",VERTEX,{"derivedFrom":[subQ1,subQ0]});Q74=makeQuery(id+"F0.imprint","IMPRINT",FACE,{"disambiguationData":[TD([[makeQuery(id+"F0.imprint","IMPRINT",EDGE,{"disambiguationData":[TD([[subQ2,-1.0]])],"derivedFrom":subQ1}),-1.0]])]});}
            var Q75;
            {var subQ0=sQuery(id+"F0.wireOp",EDGE,"E4");var subQ1=sQuery(id+"F0.wireOp",EDGE,"E1");var subQ2=makeQuery(id+"F0.imprint","INTERSECT",VERTEX,{"derivedFrom":[subQ1,subQ0]});Q75=makeQuery(id+"F0.imprint","IMPRINT",FACE,{"disambiguationData":[TD([[makeQuery(id+"F0.imprint","IMPRINT",EDGE,{"disambiguationData":[TD([[subQ2,-1.0]])],"derivedFrom":subQ1}),1.0]])]});}
            var Q76;
            {var subQ0=sQuery(id+"F0.wireOp",EDGE,"E20");var subQ1=sQuery(id+"F0.wireOp",EDGE,"E1");var subQ2=makeQuery(id+"F0.imprint","INTERSECT",VERTEX,{"derivedFrom":[subQ1,subQ0]});Q76=makeQuery(id+"F0.imprint","IMPRINT",FACE,{"disambiguationData":[TD([[makeQuery(id+"F0.imprint","IMPRINT",EDGE,{"disambiguationData":[TD([[subQ2,-1.0]])],"derivedFrom":subQ1}),1.0]])]});}
            var Q77;
            {var subQ0=sQuery(id+"F0.wireOp",EDGE,"E20");var subQ1=sQuery(id+"F0.wireOp",EDGE,"E2");var subQ2=makeQuery(id+"F0.imprint","INTERSECT",VERTEX,{"derivedFrom":[subQ1,subQ0]});Q77=makeQuery(id+"F0.imprint","IMPRINT",FACE,{"disambiguationData":[TD([[makeQuery(id+"F0.imprint","IMPRINT",EDGE,{"disambiguationData":[TD([[subQ2,-1.0]])],"derivedFrom":subQ1}),-1.0]])]});}
            extrude(context, id + "F2", {"entities" : qUnion([Q0, Q1, Q2, Q3, Q4, Q5, Q6, Q7, Q8, Q9, Q10, Q11, Q12, Q13, Q14, Q15, Q16, Q17, Q18, Q19, Q20, Q21, Q22, Q23, Q24, Q25, Q26, Q27, Q28, Q29, Q30, Q31, Q32, Q33, Q34, Q35, Q36, Q37, Q38, Q39, Q40, Q41, Q42, Q43, Q44, Q45, Q46, Q47, Q48, Q49, Q50, Q51, Q52, Q53, Q54, Q55, Q56, Q57, Q58, Q59, Q60, Q61, Q62, Q63, Q64, Q65, Q66, Q67, Q68, Q69, Q70, Q71, Q72, Q73, Q74, Q75, Q76, Q77]), "operationType" : NewBodyOperationType.ADD, "depth" : 7.9 * mm});
        }
        {
            var Q0;
            {var subQ0=sQuery(id+"F0.wireOp",EDGE,"E37");var subQ1=sQuery(id+"F0.wireOp",EDGE,"E22");var subQ2=makeQuery(id+"F0.imprint","INTERSECT",VERTEX,{"derivedFrom":[subQ1,subQ0]});Q0=makeQuery(id+"F0.imprint","IMPRINT",FACE,{"disambiguationData":[TD([[makeQuery(id+"F0.imprint","IMPRINT",EDGE,{"disambiguationData":[TD([[subQ2,-1.0]])],"derivedFrom":subQ1}),-1.0]])]});}
            var Q1;
            {var subQ0=sQuery(id+"F0.wireOp",EDGE,"E22");var subQ1=sQuery(id+"F0.wireOp",EDGE,"E16");var subQ2=makeQuery(id+"F0.imprint","INTERSECT",VERTEX,{"derivedFrom":[subQ1,subQ0]});Q1=makeQuery(id+"F0.imprint","IMPRINT",FACE,{"disambiguationData":[TD([[makeQuery(id+"F0.imprint","IMPRINT",EDGE,{"disambiguationData":[TD([[subQ2,-1.0]])],"derivedFrom":subQ1}),1.0]])]});}
            var Q2;
            {var subQ0=sQuery(id+"F0.wireOp",EDGE,"E34");var subQ1=sQuery(id+"F0.wireOp",EDGE,"E22");var subQ2=makeQuery(id+"F0.imprint","INTERSECT",VERTEX,{"derivedFrom":[subQ1,subQ0]});Q2=makeQuery(id+"F0.imprint","IMPRINT",FACE,{"disambiguationData":[TD([[makeQuery(id+"F0.imprint","IMPRINT",EDGE,{"disambiguationData":[TD([[subQ2,-1.0]])],"derivedFrom":subQ1}),-1.0]])]});}
            var Q3;
            {var subQ0=sQuery(id+"F0.wireOp",EDGE,"E22");var subQ1=sQuery(id+"F0.wireOp",EDGE,"E14");var subQ2=makeQuery(id+"F0.imprint","INTERSECT",VERTEX,{"derivedFrom":[subQ1,subQ0]});Q3=makeQuery(id+"F0.imprint","IMPRINT",FACE,{"disambiguationData":[TD([[makeQuery(id+"F0.imprint","IMPRINT",EDGE,{"disambiguationData":[TD([[subQ2,-1.0]])],"derivedFrom":subQ1}),1.0]])]});}
            var Q4;
            {var subQ0=sQuery(id+"F0.wireOp",EDGE,"E32");var subQ1=sQuery(id+"F0.wireOp",EDGE,"E22");var subQ2=makeQuery(id+"F0.imprint","INTERSECT",VERTEX,{"derivedFrom":[subQ1,subQ0]});Q4=makeQuery(id+"F0.imprint","IMPRINT",FACE,{"disambiguationData":[TD([[makeQuery(id+"F0.imprint","IMPRINT",EDGE,{"disambiguationData":[TD([[subQ2,-1.0]])],"derivedFrom":subQ1}),-1.0]])]});}
            var Q5;
            {var subQ0=sQuery(id+"F0.wireOp",EDGE,"E22");var subQ1=sQuery(id+"F0.wireOp",EDGE,"E12");var subQ2=makeQuery(id+"F0.imprint","INTERSECT",VERTEX,{"derivedFrom":[subQ1,subQ0]});Q5=makeQuery(id+"F0.imprint","IMPRINT",FACE,{"disambiguationData":[TD([[makeQuery(id+"F0.imprint","IMPRINT",EDGE,{"disambiguationData":[TD([[subQ2,-1.0]])],"derivedFrom":subQ1}),1.0]])]});}
            var Q6;
            {var subQ0=sQuery(id+"F0.wireOp",EDGE,"E31");var subQ1=sQuery(id+"F0.wireOp",EDGE,"E22");var subQ2=makeQuery(id+"F0.imprint","INTERSECT",VERTEX,{"derivedFrom":[subQ1,subQ0]});Q6=makeQuery(id+"F0.imprint","IMPRINT",FACE,{"disambiguationData":[TD([[makeQuery(id+"F0.imprint","IMPRINT",EDGE,{"disambiguationData":[TD([[subQ2,-1.0]])],"derivedFrom":subQ1}),-1.0]])]});}
            var Q7;
            {var subQ0=sQuery(id+"F0.wireOp",EDGE,"E22");var subQ1=sQuery(id+"F0.wireOp",EDGE,"E10");var subQ2=makeQuery(id+"F0.imprint","INTERSECT",VERTEX,{"derivedFrom":[subQ1,subQ0]});Q7=makeQuery(id+"F0.imprint","IMPRINT",FACE,{"disambiguationData":[TD([[makeQuery(id+"F0.imprint","IMPRINT",EDGE,{"disambiguationData":[TD([[subQ2,-1.0]])],"derivedFrom":subQ1}),1.0]])]});}
            var Q8;
            {var subQ0=sQuery(id+"F0.wireOp",EDGE,"E29");var subQ1=sQuery(id+"F0.wireOp",EDGE,"E22");var subQ2=makeQuery(id+"F0.imprint","INTERSECT",VERTEX,{"derivedFrom":[subQ1,subQ0]});Q8=makeQuery(id+"F0.imprint","IMPRINT",FACE,{"disambiguationData":[TD([[makeQuery(id+"F0.imprint","IMPRINT",EDGE,{"disambiguationData":[TD([[subQ2,-1.0]])],"derivedFrom":subQ1}),-1.0]])]});}
            var Q9;
            {var subQ0=sQuery(id+"F0.wireOp",EDGE,"E22");var subQ1=sQuery(id+"F0.wireOp",EDGE,"E8");var subQ2=makeQuery(id+"F0.imprint","INTERSECT",VERTEX,{"derivedFrom":[subQ1,subQ0]});Q9=makeQuery(id+"F0.imprint","IMPRINT",FACE,{"disambiguationData":[TD([[makeQuery(id+"F0.imprint","IMPRINT",EDGE,{"disambiguationData":[TD([[subQ2,-1.0]])],"derivedFrom":subQ1}),1.0]])]});}
            var Q10;
            {var subQ0=sQuery(id+"F0.wireOp",EDGE,"E27");var subQ1=sQuery(id+"F0.wireOp",EDGE,"E22");var subQ2=makeQuery(id+"F0.imprint","INTERSECT",VERTEX,{"derivedFrom":[subQ1,subQ0]});Q10=makeQuery(id+"F0.imprint","IMPRINT",FACE,{"disambiguationData":[TD([[makeQuery(id+"F0.imprint","IMPRINT",EDGE,{"disambiguationData":[TD([[subQ2,-1.0]])],"derivedFrom":subQ1}),-1.0]])]});}
            var Q11;
            {var subQ0=sQuery(id+"F0.wireOp",EDGE,"E22");var subQ1=sQuery(id+"F0.wireOp",EDGE,"E6");var subQ2=makeQuery(id+"F0.imprint","INTERSECT",VERTEX,{"derivedFrom":[subQ1,subQ0]});Q11=makeQuery(id+"F0.imprint","IMPRINT",FACE,{"disambiguationData":[TD([[makeQuery(id+"F0.imprint","IMPRINT",EDGE,{"disambiguationData":[TD([[subQ2,-1.0]])],"derivedFrom":subQ1}),1.0]])]});}
            var Q12;
            {var subQ0=sQuery(id+"F0.wireOp",EDGE,"E25");var subQ1=sQuery(id+"F0.wireOp",EDGE,"E22");var subQ2=makeQuery(id+"F0.imprint","INTERSECT",VERTEX,{"derivedFrom":[subQ1,subQ0]});Q12=makeQuery(id+"F0.imprint","IMPRINT",FACE,{"disambiguationData":[TD([[makeQuery(id+"F0.imprint","IMPRINT",EDGE,{"disambiguationData":[TD([[subQ2,-1.0]])],"derivedFrom":subQ1}),-1.0]])]});}
            var Q13;
            {var subQ0=sQuery(id+"F0.wireOp",EDGE,"E22");var subQ1=sQuery(id+"F0.wireOp",EDGE,"E4");var subQ2=makeQuery(id+"F0.imprint","INTERSECT",VERTEX,{"derivedFrom":[subQ1,subQ0]});Q13=makeQuery(id+"F0.imprint","IMPRINT",FACE,{"disambiguationData":[TD([[makeQuery(id+"F0.imprint","IMPRINT",EDGE,{"disambiguationData":[TD([[subQ2,-1.0]])],"derivedFrom":subQ1}),1.0]])]});}
            var Q14;
            {var subQ0=sQuery(id+"F0.wireOp",EDGE,"E22");var subQ1=sQuery(id+"F0.wireOp",EDGE,"E20");var subQ2=makeQuery(id+"F0.imprint","INTERSECT",VERTEX,{"derivedFrom":[subQ1,subQ0]});Q14=makeQuery(id+"F0.imprint","IMPRINT",FACE,{"disambiguationData":[TD([[makeQuery(id+"F0.imprint","IMPRINT",EDGE,{"disambiguationData":[TD([[subQ2,-1.0]])],"derivedFrom":subQ1}),1.0]])]});}
            extrude(context, id + "F3", {"entities" : qUnion([Q0, Q1, Q2, Q3, Q4, Q5, Q6, Q7, Q8, Q9, Q10, Q11, Q12, Q13, Q14]), "operationType" : NewBodyOperationType.ADD, "depth" : .1 * mm});
        }
    });
